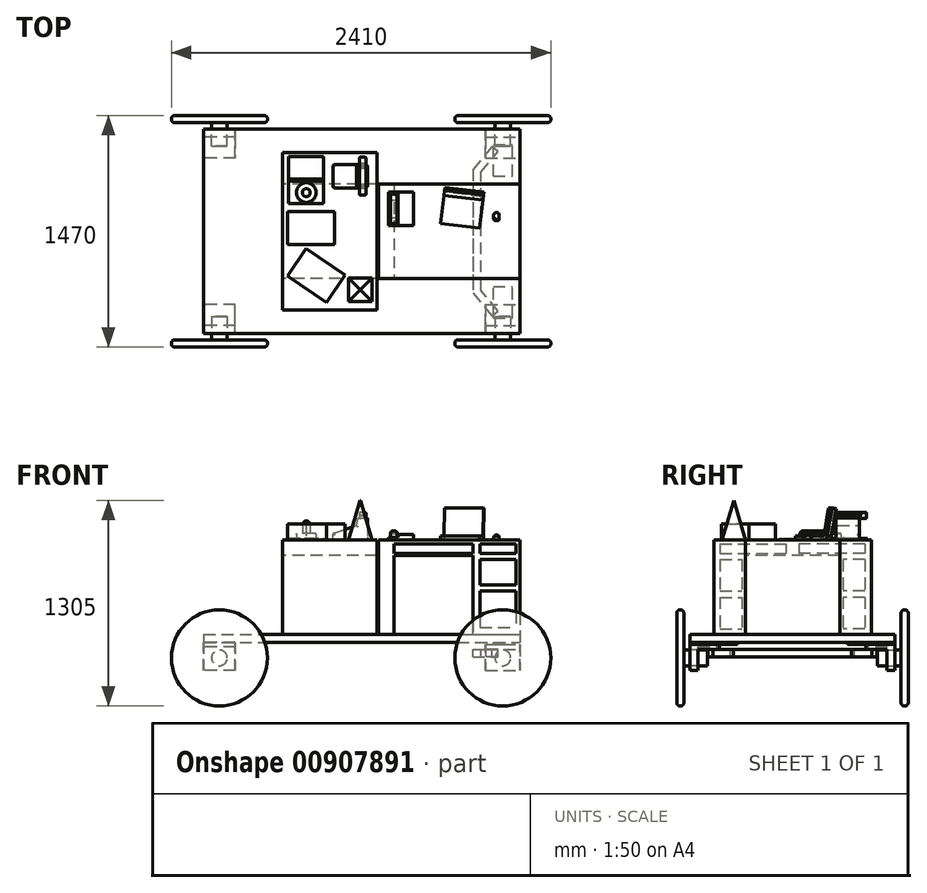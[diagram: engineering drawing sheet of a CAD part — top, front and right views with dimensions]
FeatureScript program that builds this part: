
annotation { "Feature Type Name" : "Feature", "Feature Type Description" : "" }
export const myFeature = defineFeature(function(context is Context, id is Id, definition is map)
    precondition{}
    {
        {
            var Q0;
            Q0=qCreatedBy(makeId("Top.planeOp"),FACE);
            var sketch = newSketch(context, id + "F0", { "sketchPlane" : qUnion([Q0])});
            skLineSegment(sketch, "E0.bottom", {"start": v(0, 0) * mm, "end": v(2010, 0) * mm});
            skLineSegment(sketch, "E0.top", {"start": v(0, 1300) * mm, "end": v(2010, 1300) * mm});
            skLineSegment(sketch, "E0.left", {"start": v(0, 0) * mm, "end": v(0, 1300) * mm});
            skLineSegment(sketch, "E0.right", {"start": v(2010, 0) * mm, "end": v(2010, 1300) * mm});
            skSolve(sketch);
        }
        {
            var Q0;
            Q0 = qSketchRegion(id + "F0", true);
            extrude(context, id + "F1", {"entities" : qUnion([Q0]), "depth" : 50 * mm, "offsetDistance" : 25 * mm});
        }
        {
            var Q0;
            Q0=makeQuery(id+"F1.opExtrude","CAP_FACE",FACE,{"disambiguationData":[OSD([sQuery(id+"F0.wireOp",EDGE,"E0.bottom"),sQuery(id+"F0.wireOp",EDGE,"E0.top"),sQuery(id+"F0.wireOp",EDGE,"E0.left"),sQuery(id+"F0.wireOp",EDGE,"E0.right")])],"isStart":false});
            var sketch = newSketch(context, id + "F2", { "sketchPlane" : qUnion([Q0])});
            skLineSegment(sketch, "E1.bottom", {"start": v(500, 1150) * mm, "end": v(1100, 1150) * mm});
            skLineSegment(sketch, "E1.top", {"start": v(500, 150) * mm, "end": v(1100, 150) * mm});
            skLineSegment(sketch, "E1.left", {"start": v(500, 1150) * mm, "end": v(500, 150) * mm});
            skLineSegment(sketch, "E1.right", {"start": v(1100, 1150) * mm, "end": v(1100, 150) * mm});
            skSolve(sketch);
        }
        {
            var Q0;
            Q0 = qSketchRegion(id + "F2", true);
            extrude(context, id + "F3", {"entities" : qUnion([Q0]), "depth" : 600 * mm, "offsetDistance" : 25 * mm});
        }
        {
            var Q0;
            Q0=makeQuery(id+"F1.opExtrude","CAP_FACE",FACE,{"disambiguationData":[OSD([sQuery(id+"F0.wireOp",EDGE,"E0.bottom"),sQuery(id+"F0.wireOp",EDGE,"E0.top"),sQuery(id+"F0.wireOp",EDGE,"E0.left"),sQuery(id+"F0.wireOp",EDGE,"E0.right")])],"isStart":false});
            var sketch = newSketch(context, id + "F4", { "sketchPlane" : qUnion([Q0])});
            skLineSegment(sketch, "E2.bottom", {"start": v(1110, 950) * mm, "end": v(2010, 950) * mm});
            skLineSegment(sketch, "E2.top", {"start": v(1110, 350) * mm, "end": v(2010, 350) * mm});
            skLineSegment(sketch, "E2.left", {"start": v(1110, 950) * mm, "end": v(1110, 350) * mm});
            skLineSegment(sketch, "E2.right", {"start": v(2010, 950) * mm, "end": v(2010, 350) * mm});
            skLineSegment(sketch, "E3", {"start": v(0, 650) * mm, "end": v(2380.34, 650) * mm, "construction": true});
            skSolve(sketch);
        }
        {
            var Q0;
            Q0 = qSketchRegion(id + "F4", true);
            extrude(context, id + "F5", {"entities" : qUnion([Q0]), "surfaceOperationType" : NewSurfaceOperationType.ADD, "depth" : 600 * mm, "offsetDistance" : 25 * mm});
        }
        {
            var Q0;
            Q0=makeQuery(id+"F5.opExtrude","SWEPT_FACE",FACE,{"disambiguationData":[OSD([sQuery(id+"F4.wireOp",EDGE,"E2.top")])]});
            var sketch = newSketch(context, id + "F6", { "sketchPlane" : qUnion([Q0])});
            skLineSegment(sketch, "E4.bottom", {"start": v(1210, 550) * mm, "end": v(1710, 550) * mm});
            skLineSegment(sketch, "E4.top", {"start": v(1210, 50) * mm, "end": v(1710, 50) * mm});
            skLineSegment(sketch, "E4.left", {"start": v(1210, 550) * mm, "end": v(1210, 50) * mm});
            skLineSegment(sketch, "E4.right", {"start": v(1710, 550) * mm, "end": v(1710, 50) * mm});
            skSolve(sketch);
        }
        {
            var Q0;
            Q0 = qSketchRegion(id + "F6", true);
            extrude(context, id + "F7", {"entities" : qUnion([Q0]), "operationType" : NewBodyOperationType.REMOVE, "oppositeDirection" : true, "depth" : 660 * mm, "offsetDistance" : 25 * mm});
        }
        {
            var Q0;
            Q0=makeQuery(id+"F3.opExtrude","SWEPT_FACE",FACE,{"disambiguationData":[OSD([sQuery(id+"F2.wireOp",EDGE,"E1.left")])]});
            var sketch = newSketch(context, id + "F8", { "sketchPlane" : qUnion([Q0])});
            skLineSegment(sketch, "E5.bottom", {"start": v(-950, 550) * mm, "end": v(-350, 550) * mm});
            skLineSegment(sketch, "E5.top", {"start": v(-950, 50) * mm, "end": v(-350, 50) * mm});
            skLineSegment(sketch, "E5.left", {"start": v(-950, 550) * mm, "end": v(-950, 50) * mm});
            skLineSegment(sketch, "E5.right", {"start": v(-350, 550) * mm, "end": v(-350, 50) * mm});
            skSolve(sketch);
        }
        {
            var Q0;
            Q0 = qSketchRegion(id + "F8", true);
            var Q1;
            Q1=makeQuery(id+"F3.opExtrude","SWEPT_FACE",FACE,{"disambiguationData":[OSD([sQuery(id+"F2.wireOp",EDGE,"E1.right")])]});
            extrude(context, id + "F9", {"entities" : qUnion([Q0]), "operationType" : NewBodyOperationType.REMOVE, "endBound" : BoundingType.UP_TO_SURFACE, "oppositeDirection" : true, "depth" : 25 * mm, "endBoundEntityFace" : qUnion([Q1]), "offsetDistance" : 25 * mm});
        }
        {
            var Q0;
            Q0=makeQuery(id+"F1.opExtrude","SWEPT_FACE",FACE,{"disambiguationData":[OSD([sQuery(id+"F0.wireOp",EDGE,"E0.bottom")])]});
            cPlane(context, id + "F10", {"entities" : qUnion([Q0]), "cplaneType" : CPlaneType.OFFSET, "offset" : 40 * mm, "width" : 150 * mm, "height" : 150 * mm});
        }
        {
            var Q0;
            Q0=qCreatedBy(id+"F10.planeOp",FACE);
            var sketch = newSketch(context, id + "F11", { "sketchPlane" : qUnion([Q0])});
            skCircle(sketch, "E6", {"center": v(1900, -100) * mm, "radius": 305 * mm});
            skCircle(sketch, "E7", {"center": v(100, -100) * mm, "radius": 305 * mm});
            skLineSegment(sketch, "E8", {"start": v(-294.71, -100) * mm, "end": v(2365.89, -100) * mm, "construction": true});
            skSolve(sketch);
        }
        {
            var Q0;
            Q0 = qSketchRegion(id + "F11", true);
            extrude(context, id + "F12", {"entities" : qUnion([Q0]), "depth" : 45 * mm, "offsetDistance" : 25 * mm});
        }
        {
            var Q0;
            Q0=makeQuery(id+"F1.opExtrude","SWEPT_FACE",FACE,{"disambiguationData":[OSD([sQuery(id+"F0.wireOp",EDGE,"E0.top")])]});
            cPlane(context, id + "F13", {"entities" : qUnion([Q0]), "cplaneType" : CPlaneType.OFFSET, "offset" : 40 * mm, "width" : 150 * mm, "height" : 150 * mm});
        }
        {
            var Q0;
            Q0=qCreatedBy(id+"F13.planeOp",FACE);
            var sketch = newSketch(context, id + "F14", { "sketchPlane" : qUnion([Q0])});
            skCircle(sketch, "E9", {"center": v(-1900, -100) * mm, "radius": 305 * mm});
            skCircle(sketch, "E10", {"center": v(-100, -100) * mm, "radius": 305 * mm});
            skLineSegment(sketch, "E11", {"start": v(-2469.21, -100) * mm, "end": v(345.26, -100) * mm, "construction": true});
            skSolve(sketch);
        }
        {
            var Q0;
            Q0 = qSketchRegion(id + "F14", true);
            extrude(context, id + "F15", {"entities" : qUnion([Q0]), "depth" : 45 * mm, "offsetDistance" : 25 * mm});
        }
        {
            var Q0;
            Q0=makeQuery(id+"F5.opExtrude","CAP_FACE",FACE,{"disambiguationData":[OSD([sQuery(id+"F4.wireOp",EDGE,"E2.bottom"),sQuery(id+"F4.wireOp",EDGE,"E2.top"),sQuery(id+"F4.wireOp",EDGE,"E2.left"),sQuery(id+"F4.wireOp",EDGE,"E2.right")])],"isStart":false});
            var sketch = newSketch(context, id + "F16", { "sketchPlane" : qUnion([Q0])});
            skLineSegment(sketch, "E12", {"start": v(1527.73, 898.55) * mm, "end": v(1503.73, 700) * mm});
            skLineSegment(sketch, "E13", {"start": v(1503.73, 700) * mm, "end": v(1751.92, 670) * mm});
            skLineSegment(sketch, "E14", {"start": v(1751.92, 670) * mm, "end": v(1775.92, 868.55) * mm});
            skLineSegment(sketch, "E15", {"start": v(1775.92, 868.55) * mm, "end": v(1527.73, 898.55) * mm});
            skSolve(sketch);
        }
        {
            var Q0;
            Q0 = qSketchRegion(id + "F16", true);
            extrude(context, id + "F17", {"entities" : qUnion([Q0]), "depth" : 25 * mm, "offsetDistance" : 25 * mm});
        }
        {
            var Q0;
            Q0=makeQuery(id+"F17.opExtrude","SWEPT_FACE",FACE,{"disambiguationData":[OSD([sQuery(id+"F16.wireOp",EDGE,"E14")])]});
            var sketch = newSketch(context, id + "F18", { "sketchPlane" : qUnion([Q0])});
            skLineSegment(sketch, "E16", {"start": v(1075.39, 675) * mm, "end": v(1106.03, 848.8) * mm});
            skLineSegment(sketch, "E17", {"start": v(1106.03, 848.8) * mm, "end": v(1086.34, 852.27) * mm});
            skLineSegment(sketch, "E18", {"start": v(1086.34, 852.27) * mm, "end": v(1055.08, 675) * mm});
            skLineSegment(sketch, "E19", {"start": v(1055.08, 675) * mm, "end": v(1075.39, 675) * mm});
            skSolve(sketch);
        }
        {
            var Q0;
            Q0=makeQuery(id+"F18.imprint","IMPRINT",FACE,{"disambiguationData":[TD([[makeQuery(id+"F18.imprint","IMPRINT",EDGE,{"derivedFrom":sQuery(id+"F18.wireOp",EDGE,"E16")}),1.0]])]});
            extrude(context, id + "F19", {"entities" : qUnion([Q0]), "operationType" : NewBodyOperationType.ADD, "oppositeDirection" : true, "depth" : 250 * mm, "offsetDistance" : 25 * mm});
        }
        {
            var Q0;
            Q0=makeQuery(id+"F5.opExtrude","CAP_FACE",FACE,{"disambiguationData":[OSD([sQuery(id+"F4.wireOp",EDGE,"E2.bottom"),sQuery(id+"F4.wireOp",EDGE,"E2.top"),sQuery(id+"F4.wireOp",EDGE,"E2.left"),sQuery(id+"F4.wireOp",EDGE,"E2.right")])],"isStart":false});
            var sketch = newSketch(context, id + "F20", { "sketchPlane" : qUnion([Q0])});
            skLineSegment(sketch, "E20.bottom", {"start": v(1842.34, 768.46) * mm, "end": v(1877.34, 768.46) * mm});
            skLineSegment(sketch, "E20.top", {"start": v(1842.34, 718.46) * mm, "end": v(1877.34, 718.46) * mm});
            skLineSegment(sketch, "E20.left", {"start": v(1842.34, 768.46) * mm, "end": v(1842.34, 718.46) * mm});
            skLineSegment(sketch, "E20.right", {"start": v(1877.34, 768.46) * mm, "end": v(1877.34, 718.46) * mm});
            skSolve(sketch);
        }
        {
            var Q0;
            Q0 = qSketchRegion(id + "F20", true);
            extrude(context, id + "F21", {"entities" : qUnion([Q0]), "depth" : 30 * mm, "offsetDistance" : 25 * mm});
        }
        {
            var Q0;
            Q0=makeQuery(id+"F21.opExtrude","SWEPT_EDGE",EDGE,{"disambiguationData":[OSD([sQuery(id+"F20.wireOp",EDGE,"E20.top"),sQuery(id+"F20.wireOp",EDGE,"E20.right")])]});
            var Q1;
            Q1=makeQuery(id+"F21.opExtrude","SWEPT_EDGE",EDGE,{"disambiguationData":[OSD([sQuery(id+"F20.wireOp",EDGE,"E20.top"),sQuery(id+"F20.wireOp",EDGE,"E20.left")])]});
            fillet(context, id + "F22", {"entities" : qUnion([Q0, Q1]), "radius" : 10 * mm, "tangentPropagation" : true, "allowEdgeOverflow" : false});
        }
        {
            var Q0;
            Q0=makeQuery(id+"F21.opExtrude","SWEPT_EDGE",EDGE,{"disambiguationData":[OSD([sQuery(id+"F20.wireOp",EDGE,"E20.bottom"),sQuery(id+"F20.wireOp",EDGE,"E20.right")])]});
            var Q1;
            Q1=makeQuery(id+"F21.opExtrude","SWEPT_EDGE",EDGE,{"disambiguationData":[OSD([sQuery(id+"F20.wireOp",EDGE,"E20.bottom"),sQuery(id+"F20.wireOp",EDGE,"E20.left")])]});
            fillet(context, id + "F23", {"entities" : qUnion([Q0, Q1]), "radius" : 15 * mm, "tangentPropagation" : true, "allowEdgeOverflow" : false});
        }
        {
            var Q0;
            Q0=makeQuery(id+"F21.opExtrude","CAP_FACE",FACE,{"disambiguationData":[OSD([sQuery(id+"F20.wireOp",EDGE,"E20.bottom"),sQuery(id+"F20.wireOp",EDGE,"E20.top"),sQuery(id+"F20.wireOp",EDGE,"E20.left"),sQuery(id+"F20.wireOp",EDGE,"E20.right")])],"isStart":false});
            fillet(context, id + "F24", {"entities" : qUnion([Q0]), "radius" : 15 * mm, "tangentPropagation" : true, "allowEdgeOverflow" : false});
        }
        {
            var Q0;
            Q0=makeQuery(id+"F5.opExtrude","CAP_FACE",FACE,{"disambiguationData":[OSD([sQuery(id+"F4.wireOp",EDGE,"E2.bottom"),sQuery(id+"F4.wireOp",EDGE,"E2.top"),sQuery(id+"F4.wireOp",EDGE,"E2.left"),sQuery(id+"F4.wireOp",EDGE,"E2.right")])],"isStart":false});
            var sketch = newSketch(context, id + "F25", { "sketchPlane" : qUnion([Q0])});
            skLineSegment(sketch, "E21.bottom", {"start": v(1173.15, 897.8) * mm, "end": v(1333.15, 897.8) * mm});
            skLineSegment(sketch, "E21.top", {"start": v(1173.15, 687.8) * mm, "end": v(1333.15, 687.8) * mm});
            skLineSegment(sketch, "E21.left", {"start": v(1173.15, 897.8) * mm, "end": v(1173.15, 687.8) * mm});
            skLineSegment(sketch, "E21.right", {"start": v(1333.15, 897.8) * mm, "end": v(1333.15, 687.8) * mm});
            skSolve(sketch);
        }
        {
            var Q0;
            Q0 = qSketchRegion(id + "F25", true);
            extrude(context, id + "F26", {"entities" : qUnion([Q0]), "depth" : 35 * mm, "offsetDistance" : 25 * mm});
        }
        {
            var Q0;
            Q0=makeQuery(id+"F26.opExtrude","CAP_FACE",FACE,{"disambiguationData":[OSD([sQuery(id+"F25.wireOp",EDGE,"E21.bottom"),sQuery(id+"F25.wireOp",EDGE,"E21.top"),sQuery(id+"F25.wireOp",EDGE,"E21.left"),sQuery(id+"F25.wireOp",EDGE,"E21.right")])],"isStart":false});
            var sketch = newSketch(context, id + "F27", { "sketchPlane" : qUnion([Q0])});
            skLineSegment(sketch, "E22.bottom", {"start": v(1173.15, 897.8) * mm, "end": v(1233.15, 897.8) * mm});
            skLineSegment(sketch, "E22.top", {"start": v(1173.15, 687.8) * mm, "end": v(1233.15, 687.8) * mm});
            skLineSegment(sketch, "E22.left", {"start": v(1173.15, 897.8) * mm, "end": v(1173.15, 687.8) * mm});
            skLineSegment(sketch, "E22.right", {"start": v(1233.15, 897.8) * mm, "end": v(1233.15, 687.8) * mm});
            skSolve(sketch);
        }
        {
            var Q0;
            Q0 = qSketchRegion(id + "F27", true);
            extrude(context, id + "F28", {"entities" : qUnion([Q0]), "operationType" : NewBodyOperationType.REMOVE, "oppositeDirection" : true, "depth" : 20 * mm, "offsetDistance" : 25 * mm});
        }
        {
            var Q0;
            Q0=makeQuery(id+"F28.boolean.opBoolean","COPY",FACE,{"derivedFrom":makeQuery(id+"F28.opExtrude","SWEPT_FACE",FACE,{"disambiguationData":[OSD([sQuery(id+"F27.wireOp",EDGE,"E22.right")])]})});
            cPlane(context, id + "F29", {"entities" : qUnion([Q0]), "cplaneType" : CPlaneType.OFFSET, "offset" : 5 * mm, "width" : 150 * mm, "height" : 150 * mm});
        }
        {
            var Q0;
            Q0=qCreatedBy(id+"F29.planeOp",FACE);
            var sketch = newSketch(context, id + "F30", { "sketchPlane" : qUnion([Q0])});
            skLineSegment(sketch, "E23", {"start": v(-887.8, 665) * mm, "end": v(-847.8, 665) * mm});
            skLineSegment(sketch, "E24", {"start": v(-847.8, 665) * mm, "end": v(-847.8, 690) * mm});
            skLineSegment(sketch, "E25", {"start": v(-847.8, 690) * mm, "end": v(-737.8, 690) * mm});
            skLineSegment(sketch, "E26", {"start": v(-737.8, 690) * mm, "end": v(-737.8, 665) * mm});
            skLineSegment(sketch, "E27", {"start": v(-737.8, 665) * mm, "end": v(-697.8, 665) * mm});
            skLineSegment(sketch, "E28", {"start": v(-697.8, 665) * mm, "end": v(-697.8, 705) * mm});
            skLineSegment(sketch, "E29", {"start": v(-697.8, 705) * mm, "end": v(-887.8, 705) * mm});
            skLineSegment(sketch, "E30", {"start": v(-887.8, 705) * mm, "end": v(-887.8, 665) * mm});
            skSolve(sketch);
        }
        {
            var Q0;
            Q0 = qSketchRegion(id + "F30", true);
            extrude(context, id + "F31", {"entities" : qUnion([Q0]), "depth" : 40 * mm, "offsetDistance" : 25 * mm});
        }
        {
            var Q0;
            Q0=makeQuery(id+"F31.opExtrude","SWEPT_EDGE",EDGE,{"disambiguationData":[OSD([sQuery(id+"F30.wireOp",EDGE,"E28"),sQuery(id+"F30.wireOp",EDGE,"E29")])]});
            var Q1;
            Q1=makeQuery(id+"F31.opExtrude","SWEPT_EDGE",EDGE,{"disambiguationData":[OSD([sQuery(id+"F30.wireOp",EDGE,"E29"),sQuery(id+"F30.wireOp",EDGE,"E30")])]});
            fillet(context, id + "F32", {"entities" : qUnion([Q0, Q1]), "radius" : 15 * mm, "tangentPropagation" : true, "allowEdgeOverflow" : false});
        }
        {
            var Q0;
            Q0=makeQuery(id+"F31.opExtrude","CAP_EDGE",EDGE,{"disambiguationData":[OSD([sQuery(id+"F30.wireOp",EDGE,"E29")])],"isStart":true});
            var Q1;
            Q1=makeQuery(id+"F31.opExtrude","CAP_EDGE",EDGE,{"disambiguationData":[OSD([sQuery(id+"F30.wireOp",EDGE,"E29")])],"isStart":false});
            fillet(context, id + "F33", {"entities" : qUnion([Q0, Q1]), "radius" : 10 * mm, "tangentPropagation" : true, "allowEdgeOverflow" : false});
        }
        {
            var Q0;
            Q0=makeQuery(id+"F3.opExtrude","CAP_FACE",FACE,{"disambiguationData":[OSD([sQuery(id+"F2.wireOp",EDGE,"E1.bottom"),sQuery(id+"F2.wireOp",EDGE,"E1.top"),sQuery(id+"F2.wireOp",EDGE,"E1.left"),sQuery(id+"F2.wireOp",EDGE,"E1.right")])],"isStart":false});
            var sketch = newSketch(context, id + "F34", { "sketchPlane" : qUnion([Q0])});
            skLineSegment(sketch, "E31.bottom", {"start": v(919.9, 352.6) * mm, "end": v(1069.9, 352.6) * mm});
            skLineSegment(sketch, "E31.top", {"start": v(919.9, 202.6) * mm, "end": v(1069.9, 202.6) * mm});
            skLineSegment(sketch, "E31.left", {"start": v(919.9, 352.6) * mm, "end": v(919.9, 202.6) * mm});
            skLineSegment(sketch, "E31.right", {"start": v(1069.9, 352.6) * mm, "end": v(1069.9, 202.6) * mm});
            skSolve(sketch);
        }
        {
            var Q0;
            Q0 = qSketchRegion(id + "F34", true);
            extrude(context, id + "F35", {"entities" : qUnion([Q0]), "depth" : 250 * mm, "offsetDistance" : 25 * mm, "hasDraft" : true, "draftAngle" : 16.5 * degree, "draftPullDirection" : true});
        }
        {
            var Q0;
            Q0=qCreatedBy(makeId("Front.planeOp"),FACE);
            cPlane(context, id + "F36", {"entities" : qUnion([Q0]), "cplaneType" : CPlaneType.OFFSET, "offset" : 1000 * mm, "oppositeDirection" : true, "width" : 150 * mm, "height" : 150 * mm});
        }
        {
            var Q0;
            Q0=qCreatedBy(id+"F36.planeOp",FACE);
            var sketch = newSketch(context, id + "F37", { "sketchPlane" : qUnion([Q0])});
            skLineSegment(sketch, "E32", {"start": v(1040.14, 650) * mm, "end": v(820.14, 650) * mm});
            skLineSegment(sketch, "E33", {"start": v(820.14, 650) * mm, "end": v(820.14, 690) * mm});
            skLineSegment(sketch, "E34", {"start": v(820.14, 690) * mm, "end": v(970.14, 740) * mm});
            skLineSegment(sketch, "E35", {"start": v(970.14, 740) * mm, "end": v(980.14, 790) * mm});
            skLineSegment(sketch, "E36", {"start": v(980.14, 790) * mm, "end": v(1040.14, 790) * mm});
            skLineSegment(sketch, "E37", {"start": v(1040.14, 790) * mm, "end": v(1040.14, 650) * mm});
            skSolve(sketch);
        }
        {
            var Q0;
            Q0 = qSketchRegion(id + "F37", true);
            extrude(context, id + "F38", {"entities" : qUnion([Q0]), "endBound" : BoundingType.SYMMETRIC, "depth" : 150 * mm, "offsetDistance" : 25 * mm});
        }
        {
            var Q0;
            Q0=makeQuery(id+"F38.opExtrude","SWEPT_FACE",FACE,{"disambiguationData":[OSD([sQuery(id+"F37.wireOp",EDGE,"E36")])]});
            var sketch = newSketch(context, id + "F39", { "sketchPlane" : qUnion([Q0])});
            skLineSegment(sketch, "E38.bottom", {"start": v(990.14, 1060) * mm, "end": v(1030.14, 1060) * mm});
            skLineSegment(sketch, "E38.top", {"start": v(990.14, 1050) * mm, "end": v(1030.14, 1050) * mm});
            skLineSegment(sketch, "E38.left", {"start": v(990.14, 1060) * mm, "end": v(990.14, 1050) * mm});
            skLineSegment(sketch, "E38.right", {"start": v(1030.14, 1060) * mm, "end": v(1030.14, 1050) * mm});
            skLineSegment(sketch, "E39.bottom", {"start": v(990.14, 950) * mm, "end": v(1030.14, 950) * mm});
            skLineSegment(sketch, "E39.top", {"start": v(990.14, 940) * mm, "end": v(1030.14, 940) * mm});
            skLineSegment(sketch, "E39.left", {"start": v(990.14, 950) * mm, "end": v(990.14, 940) * mm});
            skLineSegment(sketch, "E39.right", {"start": v(1030.14, 950) * mm, "end": v(1030.14, 940) * mm});
            skSolve(sketch);
        }
        {
            var Q0;
            Q0 = qSketchRegion(id + "F39", true);
            extrude(context, id + "F40", {"entities" : qUnion([Q0]), "operationType" : NewBodyOperationType.ADD, "depth" : 15 * mm, "offsetDistance" : 25 * mm});
        }
        {
            var Q0;
            Q0=makeQuery(id+"F40.opExtrude","SWEPT_FACE",FACE,{"disambiguationData":[OSD([sQuery(id+"F39.wireOp",EDGE,"E39.right")])]});
            var Q1;
            Q1=makeQuery(id+"F40.opExtrude","SWEPT_FACE",FACE,{"disambiguationData":[OSD([sQuery(id+"F39.wireOp",EDGE,"E39.left")])]});
            cPlane(context, id + "F41", {"entities" : qUnion([Q0, Q1]), "cplaneType" : CPlaneType.MID_PLANE, "offset" : 25 * mm, "width" : 150 * mm, "height" : 150 * mm});
        }
        {
            var Q0;
            Q0=qCreatedBy(id+"F41.planeOp",FACE);
            var sketch = newSketch(context, id + "F42", { "sketchPlane" : qUnion([Q0])});
            skLineSegment(sketch, "E40", {"start": v(880, 825) * mm, "end": v(880, 785) * mm});
            skLineSegment(sketch, "E41", {"start": v(880, 785) * mm, "end": v(920, 785) * mm});
            skLineSegment(sketch, "E42", {"start": v(920, 785) * mm, "end": v(920, 805) * mm});
            skLineSegment(sketch, "E43", {"start": v(920, 805) * mm, "end": v(1080, 805) * mm});
            skLineSegment(sketch, "E44", {"start": v(1080, 805) * mm, "end": v(1080, 785) * mm});
            skLineSegment(sketch, "E45", {"start": v(1080, 785) * mm, "end": v(1120, 785) * mm});
            skLineSegment(sketch, "E46", {"start": v(1120, 785) * mm, "end": v(1120, 825) * mm});
            skLineSegment(sketch, "E47", {"start": v(1120, 825) * mm, "end": v(880, 825) * mm});
            skSolve(sketch);
        }
        {
            var Q0;
            Q0 = qSketchRegion(id + "F42", true);
            extrude(context, id + "F43", {"entities" : qUnion([Q0]), "endBound" : BoundingType.SYMMETRIC, "depth" : 40 * mm, "offsetDistance" : 25 * mm});
        }
        {
            var Q0;
            Q0=makeQuery(id+"F38.opExtrude","CAP_EDGE",EDGE,{"disambiguationData":[OSD([sQuery(id+"F37.wireOp",EDGE,"E37")])],"isStart":false});
            var Q1;
            Q1=makeQuery(id+"F38.opExtrude","CAP_EDGE",EDGE,{"disambiguationData":[OSD([sQuery(id+"F37.wireOp",EDGE,"E37")])],"isStart":true});
            var Q2;
            Q2=makeQuery(id+"F38.opExtrude","CAP_EDGE",EDGE,{"disambiguationData":[OSD([sQuery(id+"F37.wireOp",EDGE,"E33")])],"isStart":false});
            var Q3;
            Q3=makeQuery(id+"F38.opExtrude","CAP_EDGE",EDGE,{"disambiguationData":[OSD([sQuery(id+"F37.wireOp",EDGE,"E33")])],"isStart":true});
            fillet(context, id + "F44", {"entities" : qUnion([Q0, Q1, Q2, Q3]), "radius" : 15 * mm, "tangentPropagation" : true, "allowEdgeOverflow" : false});
        }
        {
            var Q0;
            Q0=makeQuery(id+"F38.opExtrude","CAP_EDGE",EDGE,{"disambiguationData":[OSD([sQuery(id+"F37.wireOp",EDGE,"E34")])],"isStart":false});
            var Q1;
            Q1=makeQuery(id+"F38.opExtrude","CAP_EDGE",EDGE,{"disambiguationData":[OSD([sQuery(id+"F37.wireOp",EDGE,"E35")])],"isStart":false});
            var Q2;
            Q2=makeQuery(id+"F38.opExtrude","CAP_EDGE",EDGE,{"disambiguationData":[OSD([sQuery(id+"F37.wireOp",EDGE,"E35")])],"isStart":true});
            fillet(context, id + "F45", {"entities" : qUnion([Q0, Q1, Q2]), "radius" : 10 * mm, "tangentPropagation" : true, "allowEdgeOverflow" : false});
        }
        {
            var Q0;
            Q0=makeQuery(id+"F38.opExtrude","SWEPT_EDGE",EDGE,{"disambiguationData":[OSD([sQuery(id+"F37.wireOp",EDGE,"E36"),sQuery(id+"F37.wireOp",EDGE,"E37")])]});
            fillet(context, id + "F46", {"entities" : qUnion([Q0]), "radius" : 5 * mm, "tangentPropagation" : true, "allowEdgeOverflow" : false});
        }
        {
            var Q0;
            Q0=makeQuery(id+"F43.opExtrude","CAP_FACE",FACE,{"disambiguationData":[OSD([sQuery(id+"F42.wireOp",EDGE,"E40"),sQuery(id+"F42.wireOp",EDGE,"E41"),sQuery(id+"F42.wireOp",EDGE,"E42"),sQuery(id+"F42.wireOp",EDGE,"E43"),sQuery(id+"F42.wireOp",EDGE,"E44"),sQuery(id+"F42.wireOp",EDGE,"E45"),sQuery(id+"F42.wireOp",EDGE,"E46"),sQuery(id+"F42.wireOp",EDGE,"E47")])],"isStart":false});
            var Q1;
            Q1=makeQuery(id+"F43.opExtrude","CAP_FACE",FACE,{"disambiguationData":[OSD([sQuery(id+"F42.wireOp",EDGE,"E40"),sQuery(id+"F42.wireOp",EDGE,"E41"),sQuery(id+"F42.wireOp",EDGE,"E42"),sQuery(id+"F42.wireOp",EDGE,"E43"),sQuery(id+"F42.wireOp",EDGE,"E44"),sQuery(id+"F42.wireOp",EDGE,"E45"),sQuery(id+"F42.wireOp",EDGE,"E46"),sQuery(id+"F42.wireOp",EDGE,"E47")])],"isStart":true});
            var Q2;
            Q2=makeQuery(id+"F43.opExtrude","SWEPT_EDGE",EDGE,{"disambiguationData":[OSD([sQuery(id+"F42.wireOp",EDGE,"E40"),sQuery(id+"F42.wireOp",EDGE,"E47")])]});
            var Q3;
            Q3=makeQuery(id+"F43.opExtrude","SWEPT_EDGE",EDGE,{"disambiguationData":[OSD([sQuery(id+"F42.wireOp",EDGE,"E40"),sQuery(id+"F42.wireOp",EDGE,"E41")])]});
            var Q4;
            Q4=makeQuery(id+"F43.opExtrude","SWEPT_EDGE",EDGE,{"disambiguationData":[OSD([sQuery(id+"F42.wireOp",EDGE,"E46"),sQuery(id+"F42.wireOp",EDGE,"E47")])]});
            var Q5;
            Q5=makeQuery(id+"F43.opExtrude","SWEPT_EDGE",EDGE,{"disambiguationData":[OSD([sQuery(id+"F42.wireOp",EDGE,"E45"),sQuery(id+"F42.wireOp",EDGE,"E46")])]});
            var Q6;
            Q6=makeQuery(id+"F43.opExtrude","SWEPT_EDGE",EDGE,{"disambiguationData":[OSD([sQuery(id+"F42.wireOp",EDGE,"E41"),sQuery(id+"F42.wireOp",EDGE,"E42")])]});
            var Q7;
            Q7=makeQuery(id+"F43.opExtrude","SWEPT_EDGE",EDGE,{"disambiguationData":[OSD([sQuery(id+"F42.wireOp",EDGE,"E44"),sQuery(id+"F42.wireOp",EDGE,"E45")])]});
            fillet(context, id + "F47", {"entities" : qUnion([Q0, Q1, Q2, Q3, Q4, Q5, Q6, Q7]), "radius" : 5 * mm, "tangentPropagation" : true, "allowEdgeOverflow" : false});
        }
        {
            var Q0;
            Q0=makeQuery(id+"F3.opExtrude","SWEPT_FACE",FACE,{"disambiguationData":[OSD([sQuery(id+"F2.wireOp",EDGE,"E1.left")])]});
            cPlane(context, id + "F48", {"entities" : qUnion([Q0]), "cplaneType" : CPlaneType.OFFSET, "offset" : 150 * mm, "oppositeDirection" : true, "width" : 150 * mm, "height" : 150 * mm});
        }
        {
            var Q0;
            Q0=qCreatedBy(id+"F48.planeOp",FACE);
            var sketch = newSketch(context, id + "F49", { "sketchPlane" : qUnion([Q0])});
            skLineSegment(sketch, "E48", {"start": v(-1125.08, 650) * mm, "end": v(-1125.08, 660) * mm});
            skLineSegment(sketch, "E49", {"start": v(-1125.08, 660) * mm, "end": v(-981.42, 660) * mm});
            skArc(sketch, "E50", {"start": v(-968.73, 660) * mm, "mid": v(-975.08, 663.5) * mm, "end": v(-981.42, 660) * mm});
            skLineSegment(sketch, "E51", {"start": v(-968.73, 660) * mm, "end": v(-825.08, 660) * mm});
            skLineSegment(sketch, "E52", {"start": v(-825.08, 660) * mm, "end": v(-825.08, 650) * mm});
            skLineSegment(sketch, "E53", {"start": v(-825.08, 650) * mm, "end": v(-1125.08, 650) * mm});
            skSolve(sketch);
        }
        {
            var Q0;
            Q0 = qSketchRegion(id + "F49", true);
            extrude(context, id + "F50", {"entities" : qUnion([Q0]), "endBound" : BoundingType.SYMMETRIC, "depth" : 220 * mm, "offsetDistance" : 25 * mm});
        }
        {
            var Q0;
            Q0=makeQuery(id+"F50.opExtrude","SWEPT_FACE",FACE,{"disambiguationData":[OSD([sQuery(id+"F49.wireOp",EDGE,"E51")])]});
            var sketch = newSketch(context, id + "F51", { "sketchPlane" : qUnion([Q0])});
            skCircle(sketch, "E54", {"center": v(651.95, 895.72) * mm, "radius": 62.5 * mm});
            skSolve(sketch);
        }
        {
            var Q0;
            Q0 = qSketchRegion(id + "F51", true);
            extrude(context, id + "F52", {"entities" : qUnion([Q0]), "depth" : 30 * mm, "offsetDistance" : 25 * mm});
        }
        {
            var Q0;
            Q0=makeQuery(id+"F52.opExtrude","CAP_FACE",FACE,{"disambiguationData":[OSD([sQuery(id+"F51.wireOp",EDGE,"E54")])],"isStart":false});
            var sketch = newSketch(context, id + "F53", { "sketchPlane" : qUnion([Q0])});
            skCircle(sketch, "E55", {"center": v(651.95, 895.72) * mm, "radius": 25 * mm});
            skSolve(sketch);
        }
        {
            var Q0;
            Q0=makeQuery(id+"F53.imprint","IMPRINT",FACE,{"disambiguationData":[TD([[makeQuery(id+"F53.imprint","IMPRINT",EDGE,{"derivedFrom":sQuery(id+"F53.wireOp",EDGE,"E55")}),1.0]])]});
            extrude(context, id + "F54", {"entities" : qUnion([Q0]), "operationType" : NewBodyOperationType.ADD, "depth" : 80 * mm, "offsetDistance" : 25 * mm});
        }
        {
            var Q0;
            Q0=makeQuery(id+"F54.opExtrude","CAP_EDGE",EDGE,{"disambiguationData":[OSD([sQuery(id+"F53.wireOp",EDGE,"E55")])],"isStart":false});
            fillet(context, id + "F55", {"entities" : qUnion([Q0]), "radius" : 25 * mm, "tangentPropagation" : true, "allowEdgeOverflow" : false});
        }
        {
            var Q0;
            Q0=makeQuery(id+"F52.opExtrude","CAP_EDGE",EDGE,{"disambiguationData":[OSD([sQuery(id+"F51.wireOp",EDGE,"E54")])],"isStart":false});
            fillet(context, id + "F56", {"entities" : qUnion([Q0]), "radius" : 5 * mm, "tangentPropagation" : true, "allowEdgeOverflow" : false});
        }
        {
            var Q0;
            Q0=makeQuery(id+"F3.opExtrude","CAP_FACE",FACE,{"disambiguationData":[OSD([sQuery(id+"F2.wireOp",EDGE,"E1.bottom"),sQuery(id+"F2.wireOp",EDGE,"E1.top"),sQuery(id+"F2.wireOp",EDGE,"E1.left"),sQuery(id+"F2.wireOp",EDGE,"E1.right")])],"isStart":false});
            var sketch = newSketch(context, id + "F57", { "sketchPlane" : qUnion([Q0])});
            skLineSegment(sketch, "E56", {"start": v(649.73, 540.65) * mm, "end": v(531.85, 366.86) * mm});
            skLineSegment(sketch, "E57", {"start": v(531.85, 366.86) * mm, "end": v(780.13, 198.46) * mm});
            skLineSegment(sketch, "E58", {"start": v(780.13, 198.46) * mm, "end": v(898.01, 372.25) * mm});
            skLineSegment(sketch, "E59", {"start": v(898.01, 372.25) * mm, "end": v(649.73, 540.65) * mm});
            skSolve(sketch);
        }
        {
            var Q0;
            Q0 = qSketchRegion(id + "F57", true);
            extrude(context, id + "F58", {"entities" : qUnion([Q0]), "depth" : 100 * mm, "offsetDistance" : 25 * mm});
        }
        {
            var Q0;
            Q0=makeQuery(id+"F3.opExtrude","CAP_FACE",FACE,{"disambiguationData":[OSD([sQuery(id+"F2.wireOp",EDGE,"E1.bottom"),sQuery(id+"F2.wireOp",EDGE,"E1.top"),sQuery(id+"F2.wireOp",EDGE,"E1.left"),sQuery(id+"F2.wireOp",EDGE,"E1.right")])],"isStart":false});
            var sketch = newSketch(context, id + "F59", { "sketchPlane" : qUnion([Q0])});
            skLineSegment(sketch, "E60.bottom", {"start": v(531.76, 775.88) * mm, "end": v(831.76, 775.88) * mm});
            skLineSegment(sketch, "E60.top", {"start": v(531.76, 565.88) * mm, "end": v(831.76, 565.88) * mm});
            skLineSegment(sketch, "E60.left", {"start": v(531.76, 775.88) * mm, "end": v(531.76, 565.88) * mm});
            skLineSegment(sketch, "E60.right", {"start": v(831.76, 775.88) * mm, "end": v(831.76, 565.88) * mm});
            skSolve(sketch);
        }
        {
            var Q0;
            Q0 = qSketchRegion(id + "F59", true);
            extrude(context, id + "F60", {"entities" : qUnion([Q0]), "depth" : 1 * mm, "offsetDistance" : 25 * mm});
        }
        {
            var Q0;
            Q0=makeQuery(id+"F5.opExtrude","SWEPT_FACE",FACE,{"disambiguationData":[OSD([sQuery(id+"F4.wireOp",EDGE,"E2.top")])]});
            var sketch = newSketch(context, id + "F61", { "sketchPlane" : qUnion([Q0])});
            skLineSegment(sketch, "E61.bottom", {"start": v(1210, 625) * mm, "end": v(1710, 625) * mm});
            skLineSegment(sketch, "E61.top", {"start": v(1210, 565) * mm, "end": v(1710, 565) * mm});
            skLineSegment(sketch, "E61.left", {"start": v(1210, 625) * mm, "end": v(1210, 565) * mm});
            skLineSegment(sketch, "E61.right", {"start": v(1710, 625) * mm, "end": v(1710, 565) * mm});
            skLineSegment(sketch, "E62.0", {"start": v(1210.1, 624.9) * mm, "end": v(1709.9, 624.9) * mm});
            skLineSegment(sketch, "E62.1", {"start": v(1210.1, 624.9) * mm, "end": v(1210.1, 565.1) * mm});
            skLineSegment(sketch, "E62.2", {"start": v(1210.1, 565.1) * mm, "end": v(1709.9, 565.1) * mm});
            skLineSegment(sketch, "E62.3", {"start": v(1709.9, 624.9) * mm, "end": v(1709.9, 565.1) * mm});
            skSolve(sketch);
        }
        {
            var Q0;
            Q0 = qSketchRegion(id + "F61", true);
            extrude(context, id + "F62", {"entities" : qUnion([Q0]), "operationType" : NewBodyOperationType.REMOVE, "oppositeDirection" : true, "depth" : 1 * mm, "offsetDistance" : 25 * mm});
        }
        {
            var Q0;
            {var subQ1=sQuery(id+"F4.wireOp",EDGE,"E2.left");var subQ2=sQuery(id+"F4.wireOp",EDGE,"E2.top");Q0=makeQuery(id+"F62.boolean.opBoolean","SPLIT",FACE,{"disambiguationData":[TD([makeQuery(id+"F5.opExtrude","SWEPT_FACE",FACE,{"disambiguationData":[OSD([subQ1])]})])],"derivedFrom":makeQuery(id+"F5.opExtrude","SWEPT_FACE",FACE,{"disambiguationData":[OSD([subQ2])]})});}
            var sketch = newSketch(context, id + "F63", { "sketchPlane" : qUnion([Q0])});
            skLineSegment(sketch, "E63.bottom", {"start": v(1755, 525) * mm, "end": v(1985, 525) * mm});
            skLineSegment(sketch, "E63.top", {"start": v(1755, 365) * mm, "end": v(1985, 365) * mm});
            skLineSegment(sketch, "E63.left", {"start": v(1755, 525) * mm, "end": v(1755, 365) * mm});
            skLineSegment(sketch, "E63.right", {"start": v(1985, 525) * mm, "end": v(1985, 365) * mm});
            skLineSegment(sketch, "E64.bottom", {"start": v(1755, 325) * mm, "end": v(1985, 325) * mm});
            skLineSegment(sketch, "E64.top", {"start": v(1755, 95) * mm, "end": v(1985, 95) * mm});
            skLineSegment(sketch, "E64.left", {"start": v(1755, 325) * mm, "end": v(1755, 95) * mm});
            skLineSegment(sketch, "E64.right", {"start": v(1985, 325) * mm, "end": v(1985, 95) * mm});
            skLineSegment(sketch, "E65.bottom", {"start": v(1755, 625) * mm, "end": v(1985, 625) * mm});
            skLineSegment(sketch, "E65.top", {"start": v(1755, 565) * mm, "end": v(1985, 565) * mm});
            skLineSegment(sketch, "E65.left", {"start": v(1755, 625) * mm, "end": v(1755, 565) * mm});
            skLineSegment(sketch, "E65.right", {"start": v(1985, 625) * mm, "end": v(1985, 565) * mm});
            skLineSegment(sketch, "E66.0", {"start": v(1755.1, 624.9) * mm, "end": v(1984.9, 624.9) * mm});
            skLineSegment(sketch, "E66.1", {"start": v(1755.1, 624.9) * mm, "end": v(1755.1, 565.1) * mm});
            skLineSegment(sketch, "E66.2", {"start": v(1755.1, 565.1) * mm, "end": v(1984.9, 565.1) * mm});
            skLineSegment(sketch, "E66.3", {"start": v(1984.9, 624.9) * mm, "end": v(1984.9, 565.1) * mm});
            skLineSegment(sketch, "E67.0", {"start": v(1755.1, 524.9) * mm, "end": v(1984.9, 524.9) * mm});
            skLineSegment(sketch, "E67.1", {"start": v(1755.1, 524.9) * mm, "end": v(1755.1, 365.1) * mm});
            skLineSegment(sketch, "E67.2", {"start": v(1755.1, 365.1) * mm, "end": v(1984.9, 365.1) * mm});
            skLineSegment(sketch, "E67.3", {"start": v(1984.9, 524.9) * mm, "end": v(1984.9, 365.1) * mm});
            skLineSegment(sketch, "E68.0", {"start": v(1755.1, 324.9) * mm, "end": v(1984.9, 324.9) * mm});
            skLineSegment(sketch, "E68.1", {"start": v(1755.1, 324.9) * mm, "end": v(1755.1, 95.1) * mm});
            skLineSegment(sketch, "E68.2", {"start": v(1755.1, 95.1) * mm, "end": v(1984.9, 95.1) * mm});
            skLineSegment(sketch, "E68.3", {"start": v(1984.9, 324.9) * mm, "end": v(1984.9, 95.1) * mm});
            skSolve(sketch);
        }
        {
            var Q0;
            Q0 = qSketchRegion(id + "F63", true);
            extrude(context, id + "F64", {"entities" : qUnion([Q0]), "operationType" : NewBodyOperationType.REMOVE, "oppositeDirection" : true, "depth" : 1 * mm, "offsetDistance" : 25 * mm});
        }
        {
            var Q0;
            Q0=makeQuery(id+"F3.opExtrude","SWEPT_FACE",FACE,{"disambiguationData":[OSD([sQuery(id+"F2.wireOp",EDGE,"E1.left")])]});
            var sketch = newSketch(context, id + "F65", { "sketchPlane" : qUnion([Q0])});
            skLineSegment(sketch, "E69.bottom", {"start": v(-1110, 625) * mm, "end": v(-690, 625) * mm});
            skLineSegment(sketch, "E69.top", {"start": v(-1110, 565) * mm, "end": v(-690, 565) * mm});
            skLineSegment(sketch, "E69.left", {"start": v(-1110, 625) * mm, "end": v(-1110, 565) * mm});
            skLineSegment(sketch, "E69.right", {"start": v(-690, 625) * mm, "end": v(-690, 565) * mm});
            skLineSegment(sketch, "E70.bottom", {"start": v(-1110, 525) * mm, "end": v(-970, 525) * mm});
            skLineSegment(sketch, "E70.top", {"start": v(-1110, 325) * mm, "end": v(-970, 325) * mm});
            skLineSegment(sketch, "E70.left", {"start": v(-1110, 525) * mm, "end": v(-1110, 325) * mm});
            skLineSegment(sketch, "E70.right", {"start": v(-970, 525) * mm, "end": v(-970, 325) * mm});
            skLineSegment(sketch, "E71.bottom", {"start": v(-1110, 285) * mm, "end": v(-970, 285) * mm});
            skLineSegment(sketch, "E71.top", {"start": v(-1110, 85) * mm, "end": v(-970, 85) * mm});
            skLineSegment(sketch, "E71.left", {"start": v(-1110, 285) * mm, "end": v(-1110, 85) * mm});
            skLineSegment(sketch, "E71.right", {"start": v(-970, 285) * mm, "end": v(-970, 85) * mm});
            skLineSegment(sketch, "E72", {"start": v(-650, 550) * mm, "end": v(-650, 283.48) * mm, "construction": true});
            skLineSegment(sketch, "E73.0", {"start": v(-1109.9, 624.9) * mm, "end": v(-690.1, 624.9) * mm});
            skLineSegment(sketch, "E73.1", {"start": v(-1109.9, 624.9) * mm, "end": v(-1109.9, 565.1) * mm});
            skLineSegment(sketch, "E73.2", {"start": v(-1109.9, 565.1) * mm, "end": v(-690.1, 565.1) * mm});
            skLineSegment(sketch, "E73.3", {"start": v(-690.1, 624.9) * mm, "end": v(-690.1, 565.1) * mm});
            skLineSegment(sketch, "E74.0", {"start": v(-1109.9, 524.9) * mm, "end": v(-970.1, 524.9) * mm});
            skLineSegment(sketch, "E74.1", {"start": v(-1109.9, 524.9) * mm, "end": v(-1109.9, 325.1) * mm});
            skLineSegment(sketch, "E74.2", {"start": v(-1109.9, 325.1) * mm, "end": v(-970.1, 325.1) * mm});
            skLineSegment(sketch, "E74.3", {"start": v(-970.1, 524.9) * mm, "end": v(-970.1, 325.1) * mm});
            skLineSegment(sketch, "E75.0", {"start": v(-1109.9, 284.9) * mm, "end": v(-970.1, 284.9) * mm});
            skLineSegment(sketch, "E75.1", {"start": v(-1109.9, 284.9) * mm, "end": v(-1109.9, 85.1) * mm});
            skLineSegment(sketch, "E75.2", {"start": v(-1109.9, 85.1) * mm, "end": v(-970.1, 85.1) * mm});
            skLineSegment(sketch, "E75.3", {"start": v(-970.1, 284.9) * mm, "end": v(-970.1, 85.1) * mm});
            skLineSegment(sketch, "E76.MirrorCS", {"start": v(-609.9, 624.9) * mm, "end": v(-609.9, 565.1) * mm});
            skLineSegment(sketch, "E77.MirrorCS", {"start": v(-190, 625) * mm, "end": v(-190, 565) * mm});
            skLineSegment(sketch, "E78.MirrorCS", {"start": v(-610, 625) * mm, "end": v(-610, 565) * mm});
            skLineSegment(sketch, "E79.MirrorCS", {"start": v(-190.1, 624.9) * mm, "end": v(-190.1, 565.1) * mm});
            skLineSegment(sketch, "E80.MirrorCS", {"start": v(-190, 285) * mm, "end": v(-330, 285) * mm});
            skLineSegment(sketch, "E81.MirrorCS", {"start": v(-190, 525) * mm, "end": v(-330, 525) * mm});
            skLineSegment(sketch, "E82.MirrorCS", {"start": v(-190.1, 284.9) * mm, "end": v(-190.1, 85.1) * mm});
            skLineSegment(sketch, "E83.MirrorCS", {"start": v(-190, 625) * mm, "end": v(-610, 625) * mm});
            skLineSegment(sketch, "E84.MirrorCS", {"start": v(-329.9, 284.9) * mm, "end": v(-329.9, 85.1) * mm});
            skLineSegment(sketch, "E85.MirrorCS", {"start": v(-190, 325) * mm, "end": v(-330, 325) * mm});
            skLineSegment(sketch, "E86.MirrorCS", {"start": v(-190, 565) * mm, "end": v(-610, 565) * mm});
            skLineSegment(sketch, "E87.MirrorCS", {"start": v(-190.1, 524.9) * mm, "end": v(-329.9, 524.9) * mm});
            skLineSegment(sketch, "E88.MirrorCS", {"start": v(-190.1, 284.9) * mm, "end": v(-329.9, 284.9) * mm});
            skLineSegment(sketch, "E89.MirrorCS", {"start": v(-190, 525) * mm, "end": v(-190, 325) * mm});
            skLineSegment(sketch, "E90.MirrorCS", {"start": v(-190.1, 85.1) * mm, "end": v(-329.9, 85.1) * mm});
            skLineSegment(sketch, "E91.MirrorCS", {"start": v(-330, 525) * mm, "end": v(-330, 325) * mm});
            skLineSegment(sketch, "E92.MirrorCS", {"start": v(-190.1, 524.9) * mm, "end": v(-190.1, 325.1) * mm});
            skLineSegment(sketch, "E93.MirrorCS", {"start": v(-190.1, 325.1) * mm, "end": v(-329.9, 325.1) * mm});
            skLineSegment(sketch, "E94.MirrorCS", {"start": v(-329.9, 524.9) * mm, "end": v(-329.9, 325.1) * mm});
            skLineSegment(sketch, "E95.MirrorCS", {"start": v(-190, 285) * mm, "end": v(-190, 85) * mm});
            skLineSegment(sketch, "E96.MirrorCS", {"start": v(-330, 285) * mm, "end": v(-330, 85) * mm});
            skLineSegment(sketch, "E97.MirrorCS", {"start": v(-190.1, 565.1) * mm, "end": v(-609.9, 565.1) * mm});
            skLineSegment(sketch, "E98.MirrorCS", {"start": v(-190, 85) * mm, "end": v(-330, 85) * mm});
            skLineSegment(sketch, "E99.MirrorCS", {"start": v(-190.1, 624.9) * mm, "end": v(-609.9, 624.9) * mm});
            skSolve(sketch);
        }
        {
            var Q0;
            Q0 = qSketchRegion(id + "F65", true);
            extrude(context, id + "F66", {"entities" : qUnion([Q0]), "operationType" : NewBodyOperationType.REMOVE, "oppositeDirection" : true, "depth" : 1 * mm, "offsetDistance" : 25 * mm});
        }
        {
            var Q0;
            Q0=makeQuery(id+"F12.opExtrude","SWEPT_FACE",FACE,{"disambiguationData":[OSD([sQuery(id+"F11.wireOp",EDGE,"E7")])]});
            var Q1;
            Q1=makeQuery(id+"F12.opExtrude","SWEPT_FACE",FACE,{"disambiguationData":[OSD([sQuery(id+"F11.wireOp",EDGE,"E6")])]});
            var Q2;
            Q2=makeQuery(id+"F15.opExtrude","SWEPT_FACE",FACE,{"disambiguationData":[OSD([sQuery(id+"F14.wireOp",EDGE,"E9")])]});
            var Q3;
            Q3=makeQuery(id+"F15.opExtrude","SWEPT_FACE",FACE,{"disambiguationData":[OSD([sQuery(id+"F14.wireOp",EDGE,"E10")])]});
            fillet(context, id + "F67", {"entities" : qUnion([Q0, Q1, Q2, Q3]), "radius" : 20 * mm, "tangentPropagation" : true, "allowEdgeOverflow" : false});
        }
        {
            var Q0;
            Q0=makeQuery(id+"F15.opExtrude","CAP_FACE",FACE,{"disambiguationData":[OSD([sQuery(id+"F14.wireOp",EDGE,"E9")])],"isStart":true});
            var sketch = newSketch(context, id + "F68", { "sketchPlane" : qUnion([Q0])});
            skCircle(sketch, "E100", {"center": v(1900, -100) * mm, "radius": 50 * mm});
            skSolve(sketch);
        }
        {
            var Q0;
            Q0 = qSketchRegion(id + "F68", true);
            extrude(context, id + "F69", {"entities" : qUnion([Q0]), "depth" : 150 * mm, "offsetDistance" : 25 * mm});
        }
        {
            var Q0;
            Q0=makeQuery(id+"F12.opExtrude","CAP_FACE",FACE,{"disambiguationData":[OSD([sQuery(id+"F11.wireOp",EDGE,"E6")])],"isStart":true});
            var sketch = newSketch(context, id + "F70", { "sketchPlane" : qUnion([Q0])});
            skCircle(sketch, "E101", {"center": v(-1900, -100) * mm, "radius": 50 * mm});
            skSolve(sketch);
        }
        {
            var Q0;
            Q0 = qSketchRegion(id + "F70", true);
            extrude(context, id + "F71", {"entities" : qUnion([Q0]), "depth" : 150 * mm, "offsetDistance" : 25 * mm});
        }
        {
            var Q0;
            Q0=makeQuery(id+"F1.opExtrude","SWEPT_FACE",FACE,{"disambiguationData":[OSD([sQuery(id+"F0.wireOp",EDGE,"E0.right")])]});
            var sketch = newSketch(context, id + "F72", { "sketchPlane" : qUnion([Q0])});
            skLineSegment(sketch, "E102", {"start": v(0, -15) * mm, "end": v(0, -180) * mm});
            skLineSegment(sketch, "E103", {"start": v(0, -180) * mm, "end": v(50, -180) * mm});
            skLineSegment(sketch, "E104", {"start": v(50, -180) * mm, "end": v(50, -45) * mm});
            skLineSegment(sketch, "E105", {"start": v(50, -45) * mm, "end": v(185, -45) * mm});
            skLineSegment(sketch, "E106", {"start": v(185, -15) * mm, "end": v(0, -15) * mm});
            skLineSegment(sketch, "E107", {"start": v(1300, -15) * mm, "end": v(1300, -180) * mm});
            skLineSegment(sketch, "E108", {"start": v(1300, -180) * mm, "end": v(1250, -180) * mm});
            skLineSegment(sketch, "E109", {"start": v(1250, -180) * mm, "end": v(1250, -45) * mm});
            skLineSegment(sketch, "E110", {"start": v(1250, -45) * mm, "end": v(1115, -45) * mm});
            skLineSegment(sketch, "E111", {"start": v(1115, -45) * mm, "end": v(1115, -15) * mm});
            skLineSegment(sketch, "E112", {"start": v(1115, -15) * mm, "end": v(1300, -15) * mm});
            skLineSegment(sketch, "E113", {"start": v(185, -45) * mm, "end": v(185, -15) * mm});
            skSolve(sketch);
        }
        {
            var Q0;
            Q0 = qSketchRegion(id + "F72", true);
            extrude(context, id + "F73", {"entities" : qUnion([Q0]), "oppositeDirection" : true, "depth" : 220 * mm, "offsetDistance" : 25 * mm});
        }
        {
            var Q0;
            Q0=makeQuery(id+"F1.opExtrude","CAP_FACE",FACE,{"disambiguationData":[OSD([sQuery(id+"F0.wireOp",EDGE,"E0.bottom"),sQuery(id+"F0.wireOp",EDGE,"E0.top"),sQuery(id+"F0.wireOp",EDGE,"E0.left"),sQuery(id+"F0.wireOp",EDGE,"E0.right")])],"isStart":true});
            var sketch = newSketch(context, id + "F74", { "sketchPlane" : qUnion([Q0])});
            skLineSegment(sketch, "E114.bottom", {"start": v(1840, -100) * mm, "end": v(1960, -100) * mm});
            skLineSegment(sketch, "E114.top", {"start": v(1840, -300) * mm, "end": v(1960, -300) * mm});
            skLineSegment(sketch, "E114.left", {"start": v(1840, -100) * mm, "end": v(1840, -300) * mm});
            skLineSegment(sketch, "E114.right", {"start": v(1960, -100) * mm, "end": v(1960, -300) * mm});
            skLineSegment(sketch, "E115.bottom", {"start": v(1840, -1000) * mm, "end": v(1960, -1000) * mm});
            skLineSegment(sketch, "E115.top", {"start": v(1840, -1200) * mm, "end": v(1960, -1200) * mm});
            skLineSegment(sketch, "E115.left", {"start": v(1840, -1000) * mm, "end": v(1840, -1200) * mm});
            skLineSegment(sketch, "E115.right", {"start": v(1960, -1000) * mm, "end": v(1960, -1200) * mm});
            skSolve(sketch);
        }
        {
            var Q0;
            Q0 = qSketchRegion(id + "F74", true);
            extrude(context, id + "F75", {"entities" : qUnion([Q0]), "depth" : 15 * mm, "offsetDistance" : 25 * mm});
        }
        {
            var Q0;
            Q0=makeQuery(id+"F73.opExtrude","SWEPT_FACE",FACE,{"disambiguationData":[OSD([sQuery(id+"F72.wireOp",EDGE,"E105")])]});
            var sketch = newSketch(context, id + "F76", { "sketchPlane" : qUnion([Q0])});
            skLineSegment(sketch, "E116", {"start": v(1830.97, -112.63) * mm, "end": v(1869.27, -144.77) * mm});
            skLineSegment(sketch, "E117", {"start": v(1869.27, -144.77) * mm, "end": v(1760, -275) * mm});
            skLineSegment(sketch, "E118", {"start": v(1760, -275) * mm, "end": v(1760, -1025) * mm});
            skLineSegment(sketch, "E119", {"start": v(1760, -1025) * mm, "end": v(1869.27, -1155.23) * mm});
            skLineSegment(sketch, "E120", {"start": v(1869.27, -1155.23) * mm, "end": v(1830.97, -1187.37) * mm});
            skLineSegment(sketch, "E121", {"start": v(1830.97, -1187.37) * mm, "end": v(1710, -1043.2) * mm});
            skLineSegment(sketch, "E122", {"start": v(1710, -1043.2) * mm, "end": v(1710, -256.8) * mm});
            skLineSegment(sketch, "E123", {"start": v(1710, -256.8) * mm, "end": v(1830.97, -112.63) * mm});
            skLineSegment(sketch, "E124", {"start": v(2229.9, -650) * mm, "end": v(2010, -650) * mm, "construction": true});
            skSolve(sketch);
        }
        {
            var Q0;
            Q0 = qSketchRegion(id + "F76", true);
            extrude(context, id + "F77", {"entities" : qUnion([Q0]), "depth" : 50 * mm, "offsetDistance" : 25 * mm});
        }
        {
            var Q0;
            Q0=makeQuery(id+"F15.opExtrude","CAP_FACE",FACE,{"disambiguationData":[OSD([sQuery(id+"F14.wireOp",EDGE,"E10")])],"isStart":true});
            var sketch = newSketch(context, id + "F78", { "sketchPlane" : qUnion([Q0])});
            skCircle(sketch, "E125", {"center": v(100, -100) * mm, "radius": 50 * mm});
            skSolve(sketch);
        }
        {
            var Q0;
            Q0 = qSketchRegion(id + "F78", true);
            extrude(context, id + "F79", {"entities" : qUnion([Q0]), "depth" : 150 * mm, "offsetDistance" : 25 * mm});
        }
        {
            var Q0;
            Q0=makeQuery(id+"F12.opExtrude","CAP_FACE",FACE,{"disambiguationData":[OSD([sQuery(id+"F11.wireOp",EDGE,"E7")])],"isStart":true});
            var sketch = newSketch(context, id + "F80", { "sketchPlane" : qUnion([Q0])});
            skCircle(sketch, "E126", {"center": v(-100, -100) * mm, "radius": 50 * mm});
            skSolve(sketch);
        }
        {
            var Q0;
            Q0 = qSketchRegion(id + "F80", true);
            extrude(context, id + "F81", {"entities" : qUnion([Q0]), "depth" : 150 * mm, "offsetDistance" : 25 * mm});
        }
        {
            var Q0;
            Q0=makeQuery(id+"F1.opExtrude","SWEPT_FACE",FACE,{"disambiguationData":[OSD([sQuery(id+"F0.wireOp",EDGE,"E0.left")])]});
            var sketch = newSketch(context, id + "F82", { "sketchPlane" : qUnion([Q0])});
            skLineSegment(sketch, "E127", {"start": v(-1300, 0) * mm, "end": v(-1300, -180) * mm});
            skLineSegment(sketch, "E128", {"start": v(-1300, -180) * mm, "end": v(-1250, -180) * mm});
            skLineSegment(sketch, "E129", {"start": v(-1250, -180) * mm, "end": v(-1250, -30) * mm});
            skLineSegment(sketch, "E130", {"start": v(-1250, -30) * mm, "end": v(-1115, -30) * mm});
            skLineSegment(sketch, "E131", {"start": v(-1115, -30) * mm, "end": v(-1115, 0) * mm});
            skLineSegment(sketch, "E132", {"start": v(-1115, 0) * mm, "end": v(-1300, 0) * mm});
            skLineSegment(sketch, "E133", {"start": v(0, 0) * mm, "end": v(0, -180) * mm});
            skLineSegment(sketch, "E134", {"start": v(0, -180) * mm, "end": v(-50, -180) * mm});
            skLineSegment(sketch, "E135", {"start": v(-50, -180) * mm, "end": v(-50, -30) * mm});
            skLineSegment(sketch, "E136", {"start": v(-50, -30) * mm, "end": v(-185, -30) * mm});
            skLineSegment(sketch, "E137", {"start": v(-185, -30) * mm, "end": v(-185, 0) * mm});
            skLineSegment(sketch, "E138", {"start": v(-185, 0) * mm, "end": v(0, 0) * mm});
            skSolve(sketch);
        }
        {
            var Q0;
            Q0=makeQuery(id+"F82.imprint","IMPRINT",FACE,{"disambiguationData":[TD([[makeQuery(id+"F82.imprint","IMPRINT",EDGE,{"derivedFrom":sQuery(id+"F82.wireOp",EDGE,"E127")}),1.0]])]});
            var Q1;
            Q1=makeQuery(id+"F82.imprint","IMPRINT",FACE,{"disambiguationData":[TD([[makeQuery(id+"F82.imprint","IMPRINT",EDGE,{"derivedFrom":sQuery(id+"F82.wireOp",EDGE,"E133")}),-1.0]])]});
            extrude(context, id + "F83", {"entities" : qUnion([Q0, Q1]), "oppositeDirection" : true, "depth" : 200 * mm, "offsetDistance" : 25 * mm});
        }
    });
